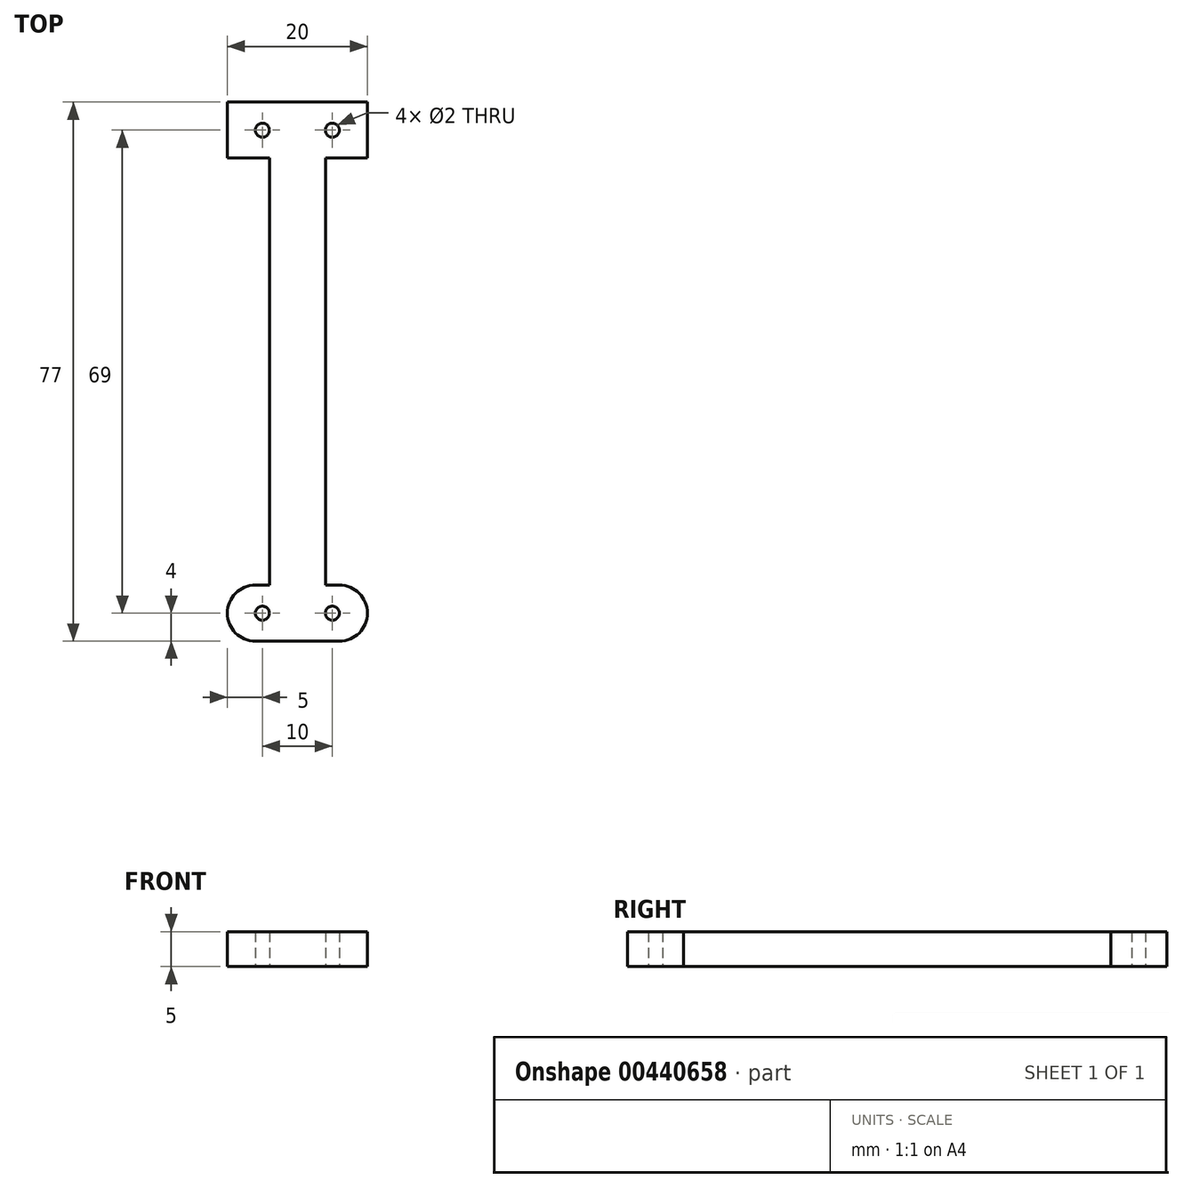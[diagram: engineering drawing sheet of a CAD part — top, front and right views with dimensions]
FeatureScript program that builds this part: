
annotation { "Feature Type Name" : "Feature", "Feature Type Description" : "" }
export const myFeature = defineFeature(function(context is Context, id is Id, definition is map)
    precondition{}
    {
        {
            var Q0;
            Q0=qCreatedBy(makeId("Top.planeOp"),FACE);
            var sketch = newSketch(context, id + "F0", { "sketchPlane" : qUnion([Q0])});
            skLineSegment(sketch, "E0.bottom", {"start": v(0, 0) * mm, "end": v(6, 0) * mm});
            skLineSegment(sketch, "E0.top", {"start": v(0, 8) * mm, "end": v(20, 8) * mm});
            skLineSegment(sketch, "E0.left", {"start": v(0, 0) * mm, "end": v(0, 8) * mm});
            skLineSegment(sketch, "E0.right", {"start": v(20, 0) * mm, "end": v(20, 8) * mm});
            skCircle(sketch, "E1", {"center": v(5, 4) * mm, "radius": 1 * mm});
            skCircle(sketch, "E2", {"center": v(15, 4) * mm, "radius": 1 * mm});
            skLineSegment(sketch, "E3.left", {"start": v(6, 0) * mm, "end": v(6, -30.5) * mm});
            skLineSegment(sketch, "E3.right", {"start": v(14, 0) * mm, "end": v(14, -30.5) * mm});
            skLineSegment(sketch, "E4.trimOffspring", {"start": v(14, 0) * mm, "end": v(20, 0) * mm});
            skLineSegment(sketch, "E5", {"start": v(6, -30.5) * mm, "end": v(14, -30.5) * mm});
            skLineSegment(sketch, "E6.MirrorCS", {"start": v(14, -61) * mm, "end": v(14, -30.5) * mm});
            skLineSegment(sketch, "E7.MirrorCS", {"start": v(6, -61) * mm, "end": v(6, -30.5) * mm});
            skLineSegment(sketch, "E8.MirrorCS", {"start": v(4, -61) * mm, "end": v(6, -61) * mm});
            skCircle(sketch, "E9.MirrorC", {"center": v(5, -65) * mm, "radius": 1 * mm});
            skCircle(sketch, "E10.MirrorC", {"center": v(15, -65) * mm, "radius": 1 * mm});
            skLineSegment(sketch, "E11.MirrorCS", {"start": v(20, -65) * mm, "end": v(20, -65) * mm});
            skLineSegment(sketch, "E12.MirrorCS", {"start": v(14, -61) * mm, "end": v(16, -61) * mm});
            skLineSegment(sketch, "E13.MirrorCS", {"start": v(4, -69) * mm, "end": v(16, -69) * mm});
            skLineSegment(sketch, "E14.MirrorCS", {"start": v(0, -65) * mm, "end": v(0, -65) * mm});
            skPoint(sketch, "E15.visualSharp", {"position": v(20, -61) * mm});
            skArc(sketch, "E15.filletArc", {"start": v(20, -65) * mm, "mid": v(18.83, -62.17) * mm, "end": v(16, -61) * mm});
            skPoint(sketch, "E16.visualSharp", {"position": v(20, -69) * mm});
            skArc(sketch, "E16.filletArc", {"start": v(16, -69) * mm, "mid": v(18.83, -67.83) * mm, "end": v(20, -65) * mm});
            skPoint(sketch, "E17.visualSharp", {"position": v(0, -69) * mm});
            skArc(sketch, "E17.filletArc", {"start": v(0, -65) * mm, "mid": v(1.17, -67.83) * mm, "end": v(4, -69) * mm});
            skPoint(sketch, "E18.visualSharp", {"position": v(0, -61) * mm});
            skArc(sketch, "E18.filletArc", {"start": v(4, -61) * mm, "mid": v(1.17, -62.17) * mm, "end": v(0, -65) * mm});
            skSolve(sketch);
        }
        {
            var Q0;
            Q0 = qSketchRegion(id + "F0", true);
            extrude(context, id + "F1", {"entities" : qUnion([Q0]), "depth" : 5 * mm});
        }
    });
